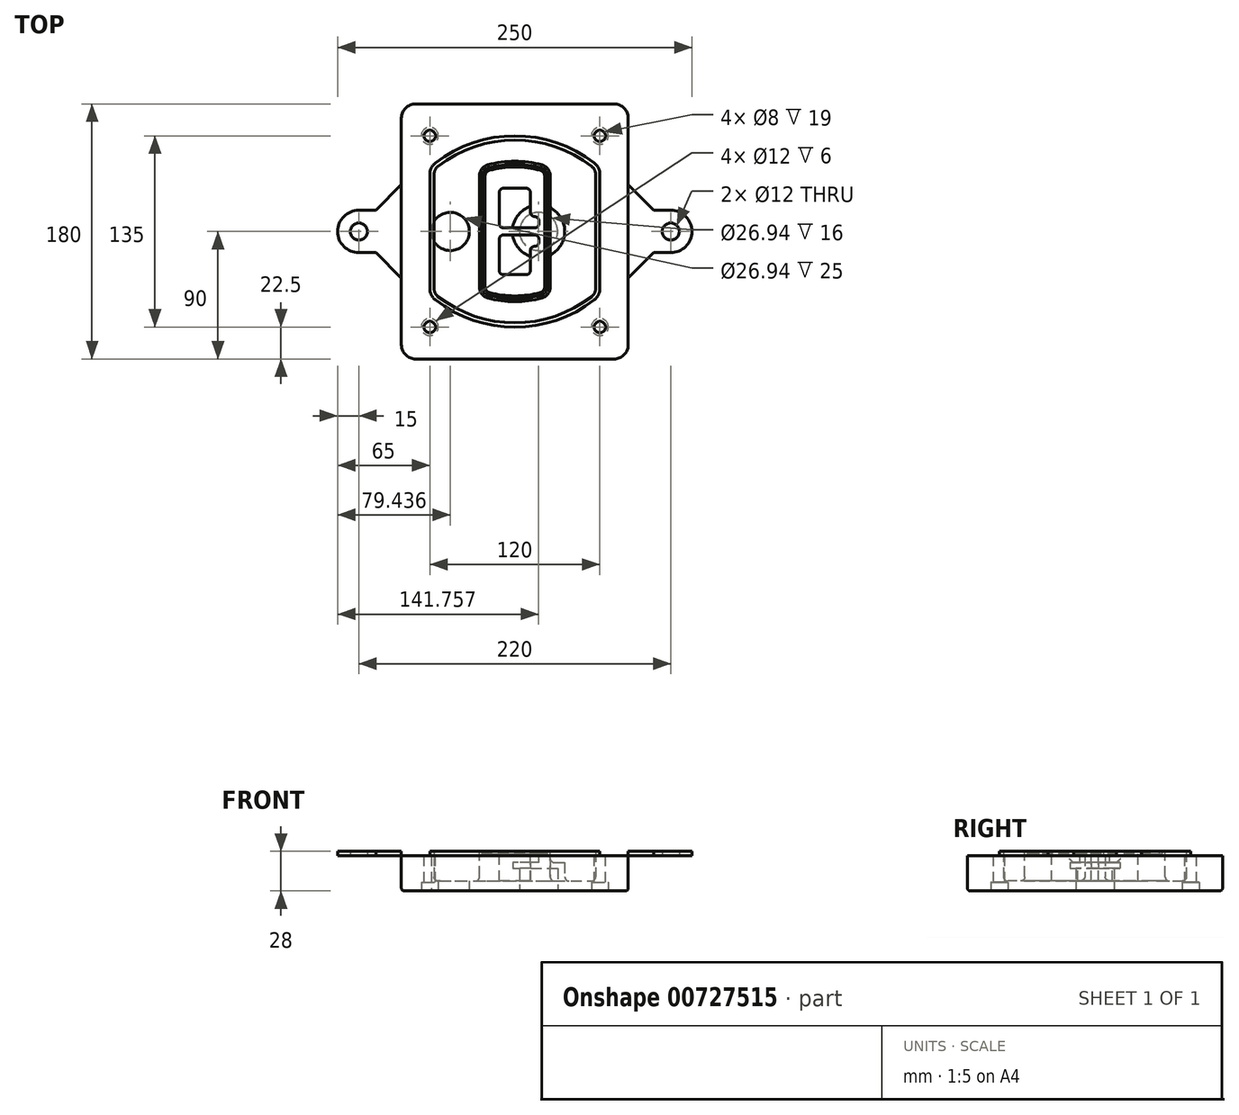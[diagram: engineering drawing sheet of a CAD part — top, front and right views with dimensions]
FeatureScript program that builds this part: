
annotation { "Feature Type Name" : "Feature", "Feature Type Description" : "" }
export const myFeature = defineFeature(function(context is Context, id is Id, definition is map)
    precondition{}
    {
        {
            var Q0;
            Q0=qCreatedBy(makeId("Top.planeOp"),FACE);
            var sketch = newSketch(context, id + "F0", { "sketchPlane" : qUnion([Q0])});
            skPoint(sketch, "E0.rect.middle", {"position": v(0, 0) * mm});
            skLineSegment(sketch, "E1.bottom", {"start": v(-70, -90) * mm, "end": v(70, -90) * mm});
            skLineSegment(sketch, "E1.top", {"start": v(-70, 90) * mm, "end": v(70, 90) * mm});
            skLineSegment(sketch, "E1.left", {"start": v(-80, -80) * mm, "end": v(-80, 80) * mm});
            skLineSegment(sketch, "E1.right", {"start": v(80, -80) * mm, "end": v(80, 80) * mm});
            skLineSegment(sketch, "E2", {"start": v(-80, 90) * mm, "end": v(80, -90) * mm, "construction": true});
            skLineSegment(sketch, "E3", {"start": v(80, 90) * mm, "end": v(-80, -90) * mm, "construction": true});
            skCircle(sketch, "E4", {"center": v(-60, 67.5) * mm, "radius": 4 * mm});
            skCircle(sketch, "E5", {"center": v(60, 67.5) * mm, "radius": 4 * mm});
            skCircle(sketch, "E6", {"center": v(60, -67.5) * mm, "radius": 4 * mm});
            skCircle(sketch, "E7", {"center": v(-60, -67.5) * mm, "radius": 4 * mm});
            skLineSegment(sketch, "E8", {"start": v(-60, 67.5) * mm, "end": v(60, 67.5) * mm, "construction": true});
            skLineSegment(sketch, "E9", {"start": v(60, 67.5) * mm, "end": v(60, -67.5) * mm, "construction": true});
            skLineSegment(sketch, "E10", {"start": v(60, -67.5) * mm, "end": v(-60, -67.5) * mm, "construction": true});
            skLineSegment(sketch, "E11", {"start": v(-60, -67.5) * mm, "end": v(-60, 67.5) * mm, "construction": true});
            skLineSegment(sketch, "E12", {"start": v(-60, 40.3) * mm, "end": v(-60, -40.3) * mm});
            skLineSegment(sketch, "E13", {"start": v(60, 40.3) * mm, "end": v(60, -40.3) * mm});
            skArc(sketch, "E14", {"start": v(56.15, 48.18) * mm, "mid": v(0, 67.5) * mm, "end": v(-56.15, 48.18) * mm});
            skArc(sketch, "E15", {"start": v(-56.15, -48.18) * mm, "mid": v(0, -67.5) * mm, "end": v(56.15, -48.18) * mm});
            skLineSegment(sketch, "E16", {"start": v(-60, 0) * mm, "end": v(60, 0) * mm, "construction": true});
            skPoint(sketch, "E17.visualSharp", {"position": v(-60, -45) * mm});
            skArc(sketch, "E17.filletArc", {"start": v(-60, -40.3) * mm, "mid": v(-58.99, -44.68) * mm, "end": v(-56.15, -48.18) * mm});
            skPoint(sketch, "E18.visualSharp", {"position": v(-60, 45) * mm});
            skArc(sketch, "E18.filletArc", {"start": v(-56.15, 48.18) * mm, "mid": v(-58.99, 44.68) * mm, "end": v(-60, 40.3) * mm});
            skPoint(sketch, "E19.visualSharp", {"position": v(60, 45) * mm});
            skArc(sketch, "E19.filletArc", {"start": v(60, 40.3) * mm, "mid": v(58.99, 44.68) * mm, "end": v(56.15, 48.18) * mm});
            skPoint(sketch, "E20.visualSharp", {"position": v(60, -45) * mm});
            skArc(sketch, "E20.filletArc", {"start": v(56.15, -48.18) * mm, "mid": v(58.99, -44.68) * mm, "end": v(60, -40.3) * mm});
            skPoint(sketch, "E21.visualSharp", {"position": v(-80, 90) * mm});
            skArc(sketch, "E21.filletArc", {"start": v(-70, 90) * mm, "mid": v(-77.07, 87.07) * mm, "end": v(-80, 80) * mm});
            skPoint(sketch, "E22.visualSharp", {"position": v(80, 90) * mm});
            skArc(sketch, "E22.filletArc", {"start": v(80, 80) * mm, "mid": v(77.07, 87.07) * mm, "end": v(70, 90) * mm});
            skPoint(sketch, "E23.visualSharp", {"position": v(80, -90) * mm});
            skArc(sketch, "E23.filletArc", {"start": v(70, -90) * mm, "mid": v(77.07, -87.07) * mm, "end": v(80, -80) * mm});
            skPoint(sketch, "E24.visualSharp", {"position": v(-80, -90) * mm});
            skArc(sketch, "E24.filletArc", {"start": v(-80, -80) * mm, "mid": v(-77.07, -87.07) * mm, "end": v(-70, -90) * mm});
            skArc(sketch, "E25.0", {"start": v(57, 40.3) * mm, "mid": v(56.3, 43.36) * mm, "end": v(54.3, 45.81) * mm});
            skLineSegment(sketch, "E25.1", {"start": v(57, 40.3) * mm, "end": v(57, -40.3) * mm});
            skArc(sketch, "E25.2", {"start": v(54.3, -45.81) * mm, "mid": v(56.3, -43.36) * mm, "end": v(57, -40.3) * mm});
            skArc(sketch, "E25.3", {"start": v(-54.3, -45.81) * mm, "mid": v(0, -64.5) * mm, "end": v(54.3, -45.81) * mm});
            skArc(sketch, "E25.4", {"start": v(-57, -40.3) * mm, "mid": v(-56.3, -43.36) * mm, "end": v(-54.3, -45.81) * mm});
            skArc(sketch, "E25.5", {"start": v(54.3, 45.81) * mm, "mid": v(0, 64.5) * mm, "end": v(-54.3, 45.81) * mm});
            skLineSegment(sketch, "E25.6", {"start": v(-57, 40.3) * mm, "end": v(-57, -40.3) * mm});
            skArc(sketch, "E25.7", {"start": v(-54.3, 45.81) * mm, "mid": v(-56.3, 43.36) * mm, "end": v(-57, 40.3) * mm});
            skArc(sketch, "E26.0", {"start": v(-58.62, 51.33) * mm, "mid": v(-62.58, 46.43) * mm, "end": v(-64, 40.3) * mm});
            skArc(sketch, "E26.1", {"start": v(58.62, 51.33) * mm, "mid": v(0, 71.5) * mm, "end": v(-58.62, 51.33) * mm});
            skArc(sketch, "E26.2", {"start": v(64, 40.3) * mm, "mid": v(62.58, 46.43) * mm, "end": v(58.62, 51.33) * mm});
            skLineSegment(sketch, "E26.3", {"start": v(64, 40.3) * mm, "end": v(64, -40.3) * mm});
            skArc(sketch, "E26.4", {"start": v(58.62, -51.33) * mm, "mid": v(62.58, -46.43) * mm, "end": v(64, -40.3) * mm});
            skLineSegment(sketch, "E26.5", {"start": v(-64, 40.3) * mm, "end": v(-64, -40.3) * mm});
            skArc(sketch, "E26.6", {"start": v(-58.62, -51.33) * mm, "mid": v(0, -71.5) * mm, "end": v(58.62, -51.33) * mm});
            skArc(sketch, "E26.7", {"start": v(-64, -40.3) * mm, "mid": v(-62.58, -46.43) * mm, "end": v(-58.62, -51.33) * mm});
            skSolve(sketch);
        }
        {
            var Q0;
            Q0=makeQuery(id+"F0.imprint","IMPRINT",FACE,{"disambiguationData":[TD([[makeQuery(id+"F0.imprint","IMPRINT",EDGE,{"derivedFrom":sQuery(id+"F0.wireOp",EDGE,"E1.bottom")}),1.0]])]});
            var Q1;
            Q1=makeQuery(id+"F0.imprint","IMPRINT",FACE,{"disambiguationData":[TD([[makeQuery(id+"F0.imprint","IMPRINT",EDGE,{"derivedFrom":sQuery(id+"F0.wireOp",EDGE,"E12")}),1.0]])]});
            var Q2;
            Q2=makeQuery(id+"F0.imprint","IMPRINT",FACE,{"disambiguationData":[TD([[makeQuery(id+"F0.imprint","IMPRINT",EDGE,{"derivedFrom":sQuery(id+"F0.wireOp",EDGE,"E25.0")}),1.0]])]});
            var Q3;
            Q3=makeQuery(id+"F0.imprint","IMPRINT",FACE,{"disambiguationData":[TD([[makeQuery(id+"F0.imprint","IMPRINT",EDGE,{"derivedFrom":sQuery(id+"F0.wireOp",EDGE,"E12")}),-1.0]])]});
            extrude(context, id + "F1", {"entities" : qUnion([Q0, Q1, Q2, Q3]), "oppositeDirection" : true, "depth" : 25 * mm});
        }
        {
            var Q0;
            Q0=makeQuery(id+"F0.imprint","IMPRINT",FACE,{"disambiguationData":[TD([[makeQuery(id+"F0.imprint","IMPRINT",EDGE,{"derivedFrom":sQuery(id+"F0.wireOp",EDGE,"E12")}),1.0]])]});
            extrude(context, id + "F2", {"entities" : qUnion([Q0]), "operationType" : NewBodyOperationType.ADD, "depth" : 3 * mm});
        }
        {
            var Q0;
            Q0=makeQuery(id+"F0.imprint","IMPRINT",FACE,{"disambiguationData":[TD([[makeQuery(id+"F0.imprint","IMPRINT",EDGE,{"derivedFrom":sQuery(id+"F0.wireOp",EDGE,"E25.0")}),1.0]])]});
            extrude(context, id + "F3", {"entities" : qUnion([Q0]), "operationType" : NewBodyOperationType.REMOVE, "oppositeDirection" : true, "depth" : 18 * mm});
        }
        {
            var Q0;
            Q0=makeQuery(id+"F2.opExtrude","CAP_FACE",FACE,{"disambiguationData":[OSD([sQuery(id+"F0.wireOp",EDGE,"E12"),sQuery(id+"F0.wireOp",EDGE,"E13"),sQuery(id+"F0.wireOp",EDGE,"E14"),sQuery(id+"F0.wireOp",EDGE,"E15"),sQuery(id+"F0.wireOp",EDGE,"E17.filletArc"),sQuery(id+"F0.wireOp",EDGE,"E18.filletArc"),sQuery(id+"F0.wireOp",EDGE,"E19.filletArc"),sQuery(id+"F0.wireOp",EDGE,"E20.filletArc"),sQuery(id+"F0.wireOp",EDGE,"E25.0"),sQuery(id+"F0.wireOp",EDGE,"E25.1"),sQuery(id+"F0.wireOp",EDGE,"E25.2"),sQuery(id+"F0.wireOp",EDGE,"E25.3"),sQuery(id+"F0.wireOp",EDGE,"E25.4"),sQuery(id+"F0.wireOp",EDGE,"E25.5"),sQuery(id+"F0.wireOp",EDGE,"E25.6"),sQuery(id+"F0.wireOp",EDGE,"E25.7")])],"isStart":false});
            var sketch = newSketch(context, id + "F4", { "sketchPlane" : qUnion([Q0])});
            skArc(sketch, "E27.0", {"start": v(-19.08, -46.97) * mm, "mid": v(0, -49.5) * mm, "end": v(19.08, -46.97) * mm});
            skArc(sketch, "E28.0", {"start": v(19.08, 46.97) * mm, "mid": v(0, 49.5) * mm, "end": v(-19.08, 46.97) * mm});
            skLineSegment(sketch, "E29", {"start": v(-25, 39.25) * mm, "end": v(-25, -39.25) * mm});
            skLineSegment(sketch, "E30", {"start": v(25, 39.25) * mm, "end": v(25, -39.25) * mm});
            skLineSegment(sketch, "E31", {"start": v(-25, 45.1) * mm, "end": v(25, 45.1) * mm, "construction": true});
            skLineSegment(sketch, "E32", {"start": v(-25, -45.1) * mm, "end": v(25, -45.1) * mm, "construction": true});
            skPoint(sketch, "E33.visualSharp", {"position": v(-25, 45.1) * mm});
            skArc(sketch, "E33.filletArc", {"start": v(-19.08, 46.97) * mm, "mid": v(-23.35, 44.11) * mm, "end": v(-25, 39.25) * mm});
            skPoint(sketch, "E34.visualSharp", {"position": v(25, 45.1) * mm});
            skArc(sketch, "E34.filletArc", {"start": v(25, 39.25) * mm, "mid": v(23.35, 44.11) * mm, "end": v(19.08, 46.97) * mm});
            skPoint(sketch, "E35.visualSharp", {"position": v(25, -45.1) * mm});
            skArc(sketch, "E35.filletArc", {"start": v(19.08, -46.97) * mm, "mid": v(23.35, -44.11) * mm, "end": v(25, -39.25) * mm});
            skPoint(sketch, "E36.visualSharp", {"position": v(-25, -45.1) * mm});
            skArc(sketch, "E36.filletArc", {"start": v(-25, -39.25) * mm, "mid": v(-23.35, -44.11) * mm, "end": v(-19.08, -46.97) * mm});
            skArc(sketch, "E37.0", {"start": v(54.3, 45.81) * mm, "mid": v(0, 64.5) * mm, "end": v(-54.3, 45.81) * mm});
            skArc(sketch, "E37.1", {"start": v(-54.3, 45.81) * mm, "mid": v(-56.3, 43.36) * mm, "end": v(-57, 40.3) * mm});
            skLineSegment(sketch, "E37.2", {"start": v(-57, 40.3) * mm, "end": v(-57, -40.3) * mm});
            skArc(sketch, "E37.3", {"start": v(-57, -40.3) * mm, "mid": v(-56.3, -43.36) * mm, "end": v(-54.3, -45.81) * mm});
            skArc(sketch, "E37.4", {"start": v(-54.3, -45.81) * mm, "mid": v(0, -64.5) * mm, "end": v(54.3, -45.81) * mm});
            skArc(sketch, "E37.5", {"start": v(54.3, -45.81) * mm, "mid": v(56.3, -43.36) * mm, "end": v(57, -40.3) * mm});
            skLineSegment(sketch, "E37.6", {"start": v(57, 40.3) * mm, "end": v(57, -40.3) * mm});
            skArc(sketch, "E37.7", {"start": v(57, 40.3) * mm, "mid": v(56.3, 43.36) * mm, "end": v(54.3, 45.81) * mm});
            skLineSegment(sketch, "E38.0", {"start": v(23, 39.25) * mm, "end": v(23, -39.25) * mm});
            skArc(sketch, "E38.1", {"start": v(18.56, -45.04) * mm, "mid": v(21.76, -42.9) * mm, "end": v(23, -39.25) * mm});
            skArc(sketch, "E38.2", {"start": v(-18.56, -45.04) * mm, "mid": v(0, -47.5) * mm, "end": v(18.56, -45.04) * mm});
            skArc(sketch, "E38.3", {"start": v(-23, -39.25) * mm, "mid": v(-21.76, -42.9) * mm, "end": v(-18.56, -45.04) * mm});
            skLineSegment(sketch, "E38.4", {"start": v(-23, 39.25) * mm, "end": v(-23, -39.25) * mm});
            skArc(sketch, "E38.5", {"start": v(23, 39.25) * mm, "mid": v(21.76, 42.9) * mm, "end": v(18.56, 45.04) * mm});
            skArc(sketch, "E38.6", {"start": v(-18.56, 45.04) * mm, "mid": v(-21.76, 42.9) * mm, "end": v(-23, 39.25) * mm});
            skArc(sketch, "E38.7", {"start": v(18.56, 45.04) * mm, "mid": v(0, 47.5) * mm, "end": v(-18.56, 45.04) * mm});
            skArc(sketch, "E39.0", {"start": v(21, 39.25) * mm, "mid": v(20.18, 41.68) * mm, "end": v(18.04, 43.1) * mm});
            skLineSegment(sketch, "E39.1", {"start": v(21, 39.25) * mm, "end": v(21, -39.25) * mm});
            skArc(sketch, "E39.2", {"start": v(18.04, -43.1) * mm, "mid": v(20.18, -41.68) * mm, "end": v(21, -39.25) * mm});
            skArc(sketch, "E39.3", {"start": v(-18.04, -43.1) * mm, "mid": v(0, -45.5) * mm, "end": v(18.04, -43.1) * mm});
            skArc(sketch, "E39.4", {"start": v(-21, -39.25) * mm, "mid": v(-20.18, -41.68) * mm, "end": v(-18.04, -43.1) * mm});
            skArc(sketch, "E39.5", {"start": v(18.04, 43.1) * mm, "mid": v(0, 45.5) * mm, "end": v(-18.04, 43.1) * mm});
            skLineSegment(sketch, "E39.6", {"start": v(-21, 39.25) * mm, "end": v(-21, -39.25) * mm});
            skArc(sketch, "E39.7", {"start": v(-18.04, 43.1) * mm, "mid": v(-20.18, 41.68) * mm, "end": v(-21, 39.25) * mm});
            skLineSegment(sketch, "E40", {"start": v(-25, 0) * mm, "end": v(25, 0) * mm, "construction": true});
            skLineSegment(sketch, "E41", {"start": v(-11, 5.5) * mm, "end": v(-11, 27.5) * mm});
            skLineSegment(sketch, "E42", {"start": v(-8, 30.5) * mm, "end": v(8, 30.5) * mm});
            skLineSegment(sketch, "E43", {"start": v(11, 27.5) * mm, "end": v(11, 13.5) * mm});
            skLineSegment(sketch, "E44", {"start": v(14, 10.5) * mm, "end": v(14, 10.5) * mm});
            skLineSegment(sketch, "E45", {"start": v(17, 7.5) * mm, "end": v(17, 5.5) * mm});
            skLineSegment(sketch, "E46", {"start": v(14, 2.5) * mm, "end": v(-8, 2.5) * mm});
            skPoint(sketch, "E47.visualSharp", {"position": v(-11, 30.5) * mm});
            skArc(sketch, "E47.filletArc", {"start": v(-8, 30.5) * mm, "mid": v(-10.12, 29.62) * mm, "end": v(-11, 27.5) * mm});
            skPoint(sketch, "E48.visualSharp", {"position": v(11, 30.5) * mm});
            skArc(sketch, "E48.filletArc", {"start": v(11, 27.5) * mm, "mid": v(10.12, 29.62) * mm, "end": v(8, 30.5) * mm});
            skPoint(sketch, "E49.visualSharp", {"position": v(11, 10.5) * mm});
            skArc(sketch, "E49.filletArc", {"start": v(11, 13.5) * mm, "mid": v(11.88, 11.38) * mm, "end": v(14, 10.5) * mm});
            skPoint(sketch, "E50.visualSharp", {"position": v(17, 10.5) * mm});
            skArc(sketch, "E50.filletArc", {"start": v(17, 7.5) * mm, "mid": v(16.12, 9.62) * mm, "end": v(14, 10.5) * mm});
            skPoint(sketch, "E51.visualSharp", {"position": v(17, 2.5) * mm});
            skArc(sketch, "E51.filletArc", {"start": v(14, 2.5) * mm, "mid": v(16.12, 3.38) * mm, "end": v(17, 5.5) * mm});
            skPoint(sketch, "E52.visualSharp", {"position": v(-11, 2.5) * mm});
            skArc(sketch, "E52.filletArc", {"start": v(-11, 5.5) * mm, "mid": v(-10.12, 3.38) * mm, "end": v(-8, 2.5) * mm});
            skLineSegment(sketch, "E53.0.MirrorCS", {"start": v(14, -2.5) * mm, "end": v(-8, -2.5) * mm});
            skArc(sketch, "E54.0.MirrorCS", {"start": v(-11, -5.5) * mm, "mid": v(-10.12, -3.38) * mm, "end": v(-8, -2.5) * mm});
            skLineSegment(sketch, "E55.0.MirrorCS", {"start": v(-11, -5.5) * mm, "end": v(-11, -27.5) * mm});
            skArc(sketch, "E56.0.MirrorCS", {"start": v(-8, -30.5) * mm, "mid": v(-10.12, -29.62) * mm, "end": v(-11, -27.5) * mm});
            skLineSegment(sketch, "E57.0.MirrorCS", {"start": v(-8, -30.5) * mm, "end": v(8, -30.5) * mm});
            skArc(sketch, "E58.0.MirrorCS", {"start": v(11, -27.5) * mm, "mid": v(10.12, -29.62) * mm, "end": v(8, -30.5) * mm});
            skLineSegment(sketch, "E59.0.MirrorCS", {"start": v(11, -27.5) * mm, "end": v(11, -13.5) * mm});
            skArc(sketch, "E60.0.MirrorCS", {"start": v(11, -13.5) * mm, "mid": v(11.88, -11.38) * mm, "end": v(14, -10.5) * mm});
            skArc(sketch, "E61.0.MirrorCS", {"start": v(17, -7.5) * mm, "mid": v(16.12, -9.62) * mm, "end": v(14, -10.5) * mm});
            skLineSegment(sketch, "E62.0.MirrorCS", {"start": v(17, -7.5) * mm, "end": v(17, -5.5) * mm});
            skArc(sketch, "E63.0.MirrorCS", {"start": v(14, -2.5) * mm, "mid": v(16.12, -3.38) * mm, "end": v(17, -5.5) * mm});
            skSolve(sketch);
        }
        {
            var Q0;
            Q0=makeQuery(id+"F4.imprint","IMPRINT",FACE,{"disambiguationData":[TD([[makeQuery(id+"F4.imprint","IMPRINT",EDGE,{"derivedFrom":sQuery(id+"F4.wireOp",EDGE,"E27.0")}),1.0]])]});
            var Q1;
            Q1=makeQuery(id+"F4.imprint","IMPRINT",FACE,{"disambiguationData":[TD([[makeQuery(id+"F4.imprint","IMPRINT",EDGE,{"derivedFrom":sQuery(id+"F4.wireOp",EDGE,"E38.0")}),-1.0]])]});
            var Q2;
            Q2=makeQuery(id+"F4.imprint","IMPRINT",FACE,{"disambiguationData":[TD([[makeQuery(id+"F4.imprint","IMPRINT",EDGE,{"derivedFrom":sQuery(id+"F4.wireOp",EDGE,"E39.0")}),1.0]])]});
            extrude(context, id + "F5", {"entities" : qUnion([Q0, Q1, Q2]), "operationType" : NewBodyOperationType.ADD, "endBound" : BoundingType.UP_TO_NEXT, "oppositeDirection" : true, "depth" : 25 * mm});
        }
        {
            var Q0;
            Q0=makeQuery(id+"F4.imprint","IMPRINT",FACE,{"disambiguationData":[TD([[makeQuery(id+"F4.imprint","IMPRINT",EDGE,{"derivedFrom":sQuery(id+"F4.wireOp",EDGE,"E38.0")}),-1.0]])]});
            extrude(context, id + "F6", {"entities" : qUnion([Q0]), "operationType" : NewBodyOperationType.REMOVE, "oppositeDirection" : true, "depth" : 2 * mm});
        }
        {
            var Q0;
            Q0=makeQuery(id+"F1.opExtrude","CAP_FACE",FACE,{"disambiguationData":[OSD([sQuery(id+"F0.wireOp",EDGE,"E1.bottom"),sQuery(id+"F0.wireOp",EDGE,"E1.top"),sQuery(id+"F0.wireOp",EDGE,"E1.left"),sQuery(id+"F0.wireOp",EDGE,"E1.right"),sQuery(id+"F0.wireOp",EDGE,"E4"),sQuery(id+"F0.wireOp",EDGE,"E5"),sQuery(id+"F0.wireOp",EDGE,"E6"),sQuery(id+"F0.wireOp",EDGE,"E7"),sQuery(id+"F0.wireOp",EDGE,"E21.filletArc"),sQuery(id+"F0.wireOp",EDGE,"E22.filletArc"),sQuery(id+"F0.wireOp",EDGE,"E23.filletArc"),sQuery(id+"F0.wireOp",EDGE,"E24.filletArc")])],"isStart":false});
            var sketch = newSketch(context, id + "F7", { "sketchPlane" : qUnion([Q0])});
            skCircle(sketch, "E64", {"center": v(16.76, 0) * mm, "radius": 13.47 * mm});
            skCircle(sketch, "E65", {"center": v(-45.56, 0) * mm, "radius": 13.47 * mm});
            skLineSegment(sketch, "E66", {"start": v(80, 0) * mm, "end": v(-80, 0) * mm});
            skCircle(sketch, "E67", {"center": v(16.76, 0) * mm, "radius": 18.47 * mm});
            skCircle(sketch, "E68", {"center": v(60, -67.5) * mm, "radius": 6 * mm});
            skCircle(sketch, "E69", {"center": v(-60, -67.5) * mm, "radius": 6 * mm});
            skCircle(sketch, "E70", {"center": v(-60, 67.5) * mm, "radius": 6 * mm});
            skCircle(sketch, "E71", {"center": v(60, 67.5) * mm, "radius": 6 * mm});
            skSolve(sketch);
        }
        {
            var Q0;
            {var subQ1=sQuery(id+"F7.wireOp",EDGE,"E66");var subQ4=sQuery(id+"F7.wireOp",EDGE,"E64");var subQ6=makeQuery(id+"F7.imprint","INTERSECT",VERTEX,{"disambiguationData":[OD(0.0)],"derivedFrom":[subQ4,subQ1]});Q0=makeQuery(id+"F7.imprint","IMPRINT",FACE,{"disambiguationData":[TD([[makeQuery(id+"F7.imprint","IMPRINT",EDGE,{"disambiguationData":[TD([[subQ6,-1.0]])],"derivedFrom":subQ4}),-1.0]])]});}
            var Q1;
            {var subQ0=sQuery(id+"F7.wireOp",EDGE,"E66");var subQ1=sQuery(id+"F7.wireOp",EDGE,"E64");var subQ3=makeQuery(id+"F7.imprint","INTERSECT",VERTEX,{"disambiguationData":[OD(0.0)],"derivedFrom":[subQ1,subQ0]});Q1=makeQuery(id+"F7.imprint","IMPRINT",FACE,{"disambiguationData":[TD([[makeQuery(id+"F7.imprint","IMPRINT",EDGE,{"disambiguationData":[TD([[subQ3,-1.0]])],"derivedFrom":subQ1}),1.0]])]});}
            var Q2;
            {var subQ0=sQuery(id+"F7.wireOp",EDGE,"E66");var subQ1=sQuery(id+"F7.wireOp",EDGE,"E64");var subQ3=makeQuery(id+"F7.imprint","INTERSECT",VERTEX,{"disambiguationData":[OD(0.0)],"derivedFrom":[subQ1,subQ0]});Q2=makeQuery(id+"F7.imprint","IMPRINT",FACE,{"disambiguationData":[TD([[makeQuery(id+"F7.imprint","IMPRINT",EDGE,{"disambiguationData":[TD([[subQ3,1.0]])],"derivedFrom":subQ1}),1.0]])]});}
            var Q3;
            {var subQ1=sQuery(id+"F7.wireOp",EDGE,"E66");var subQ4=sQuery(id+"F7.wireOp",EDGE,"E64");var subQ6=makeQuery(id+"F7.imprint","INTERSECT",VERTEX,{"disambiguationData":[OD(0.0)],"derivedFrom":[subQ4,subQ1]});Q3=makeQuery(id+"F7.imprint","IMPRINT",FACE,{"disambiguationData":[TD([[makeQuery(id+"F7.imprint","IMPRINT",EDGE,{"disambiguationData":[TD([[subQ6,1.0]])],"derivedFrom":subQ4}),-1.0]])]});}
            extrude(context, id + "F8", {"entities" : qUnion([Q0, Q1, Q2, Q3]), "operationType" : NewBodyOperationType.ADD, "oppositeDirection" : true, "depth" : 20 * mm});
        }
        {
            var Q0;
            {var subQ0=sQuery(id+"F7.wireOp",EDGE,"E66");var subQ1=sQuery(id+"F7.wireOp",EDGE,"E64");var subQ3=makeQuery(id+"F7.imprint","INTERSECT",VERTEX,{"disambiguationData":[OD(0.0)],"derivedFrom":[subQ1,subQ0]});Q0=makeQuery(id+"F7.imprint","IMPRINT",FACE,{"disambiguationData":[TD([[makeQuery(id+"F7.imprint","IMPRINT",EDGE,{"disambiguationData":[TD([[subQ3,-1.0]])],"derivedFrom":subQ1}),1.0]])]});}
            var Q1;
            {var subQ0=sQuery(id+"F7.wireOp",EDGE,"E66");var subQ1=sQuery(id+"F7.wireOp",EDGE,"E64");var subQ3=makeQuery(id+"F7.imprint","INTERSECT",VERTEX,{"disambiguationData":[OD(0.0)],"derivedFrom":[subQ1,subQ0]});Q1=makeQuery(id+"F7.imprint","IMPRINT",FACE,{"disambiguationData":[TD([[makeQuery(id+"F7.imprint","IMPRINT",EDGE,{"disambiguationData":[TD([[subQ3,1.0]])],"derivedFrom":subQ1}),1.0]])]});}
            extrude(context, id + "F9", {"entities" : qUnion([Q0, Q1]), "operationType" : NewBodyOperationType.REMOVE, "oppositeDirection" : true, "depth" : 16 * mm});
        }
        {
            var Q0;
            {var subQ0=sQuery(id+"F7.wireOp",EDGE,"E66");var subQ1=sQuery(id+"F7.wireOp",EDGE,"E65");var subQ3=makeQuery(id+"F7.imprint","INTERSECT",VERTEX,{"disambiguationData":[OD(0.0)],"derivedFrom":[subQ1,subQ0]});Q0=makeQuery(id+"F7.imprint","IMPRINT",FACE,{"disambiguationData":[TD([[makeQuery(id+"F7.imprint","IMPRINT",EDGE,{"disambiguationData":[TD([[subQ3,-1.0]])],"derivedFrom":subQ1}),1.0]])]});}
            var Q1;
            {var subQ0=sQuery(id+"F7.wireOp",EDGE,"E66");var subQ1=sQuery(id+"F7.wireOp",EDGE,"E65");var subQ3=makeQuery(id+"F7.imprint","INTERSECT",VERTEX,{"disambiguationData":[OD(0.0)],"derivedFrom":[subQ1,subQ0]});Q1=makeQuery(id+"F7.imprint","IMPRINT",FACE,{"disambiguationData":[TD([[makeQuery(id+"F7.imprint","IMPRINT",EDGE,{"disambiguationData":[TD([[subQ3,1.0]])],"derivedFrom":subQ1}),1.0]])]});}
            extrude(context, id + "F10", {"entities" : qUnion([Q0, Q1]), "operationType" : NewBodyOperationType.REMOVE, "oppositeDirection" : true, "depth" : 25 * mm});
        }
        {
            var Q0;
            Q0=makeQuery(id+"F7.imprint","IMPRINT",FACE,{"disambiguationData":[TD([[makeQuery(id+"F7.imprint","IMPRINT",EDGE,{"derivedFrom":sQuery(id+"F7.wireOp",EDGE,"E68")}),1.0]])]});
            var Q1;
            Q1=makeQuery(id+"F7.imprint","IMPRINT",FACE,{"disambiguationData":[TD([[makeQuery(id+"F7.imprint","IMPRINT",EDGE,{"derivedFrom":makeQuery(id+"F1.opExtrude","CAP_EDGE",EDGE,{"disambiguationData":[OSD([sQuery(id+"F0.wireOp",EDGE,"E5")])],"isStart":false})}),-1.0]])]});
            var Q2;
            Q2=makeQuery(id+"F7.imprint","IMPRINT",FACE,{"disambiguationData":[TD([[makeQuery(id+"F7.imprint","IMPRINT",EDGE,{"derivedFrom":sQuery(id+"F7.wireOp",EDGE,"E69")}),1.0]])]});
            var Q3;
            Q3=makeQuery(id+"F7.imprint","IMPRINT",FACE,{"disambiguationData":[TD([[makeQuery(id+"F7.imprint","IMPRINT",EDGE,{"derivedFrom":makeQuery(id+"F1.opExtrude","CAP_EDGE",EDGE,{"disambiguationData":[OSD([sQuery(id+"F0.wireOp",EDGE,"E4")])],"isStart":false})}),-1.0]])]});
            var Q4;
            Q4=makeQuery(id+"F7.imprint","IMPRINT",FACE,{"disambiguationData":[TD([[makeQuery(id+"F7.imprint","IMPRINT",EDGE,{"derivedFrom":sQuery(id+"F7.wireOp",EDGE,"E70")}),1.0]])]});
            var Q5;
            Q5=makeQuery(id+"F7.imprint","IMPRINT",FACE,{"disambiguationData":[TD([[makeQuery(id+"F7.imprint","IMPRINT",EDGE,{"derivedFrom":makeQuery(id+"F1.opExtrude","CAP_EDGE",EDGE,{"disambiguationData":[OSD([sQuery(id+"F0.wireOp",EDGE,"E7")])],"isStart":false})}),-1.0]])]});
            var Q6;
            Q6=makeQuery(id+"F7.imprint","IMPRINT",FACE,{"disambiguationData":[TD([[makeQuery(id+"F7.imprint","IMPRINT",EDGE,{"derivedFrom":sQuery(id+"F7.wireOp",EDGE,"E71")}),1.0]])]});
            var Q7;
            Q7=makeQuery(id+"F7.imprint","IMPRINT",FACE,{"disambiguationData":[TD([[makeQuery(id+"F7.imprint","IMPRINT",EDGE,{"derivedFrom":makeQuery(id+"F1.opExtrude","CAP_EDGE",EDGE,{"disambiguationData":[OSD([sQuery(id+"F0.wireOp",EDGE,"E6")])],"isStart":false})}),-1.0]])]});
            extrude(context, id + "F11", {"entities" : qUnion([Q0, Q1, Q2, Q3, Q4, Q5, Q6, Q7]), "operationType" : NewBodyOperationType.REMOVE, "oppositeDirection" : true, "depth" : 6 * mm});
        }
        {
            var Q0;
            Q0=makeQuery(id+"F9.boolean.opBoolean","COPY",FACE,{"derivedFrom":makeQuery(id+"F9.opExtrude","CAP_FACE",FACE,{"disambiguationData":[OSD([sQuery(id+"F7.wireOp",EDGE,"E64")])],"isStart":false})});
            var sketch = newSketch(context, id + "F12", { "sketchPlane" : qUnion([Q0])});
            skArc(sketch, "E72.0", {"start": v(11, 17.55) * mm, "mid": v(2.57, 11.82) * mm, "end": v(-1.54, 2.5) * mm});
            skArc(sketch, "E72.1", {"start": v(-1.54, -2.5) * mm, "mid": v(2.57, -11.82) * mm, "end": v(11, -17.55) * mm});
            skLineSegment(sketch, "E73", {"start": v(-1.54, -2.5) * mm, "end": v(14, -2.5) * mm});
            skLineSegment(sketch, "E74.0", {"start": v(14, 2.5) * mm, "end": v(-1.54, 2.5) * mm});
            skArc(sketch, "E74.1", {"start": v(14, 2.5) * mm, "mid": v(16.12, 3.38) * mm, "end": v(17, 5.5) * mm});
            skLineSegment(sketch, "E74.2", {"start": v(17, 7.5) * mm, "end": v(17, 5.5) * mm});
            skArc(sketch, "E74.3", {"start": v(17, 7.5) * mm, "mid": v(16.12, 9.62) * mm, "end": v(14, 10.5) * mm});
            skArc(sketch, "E74.4", {"start": v(11, 13.5) * mm, "mid": v(11.88, 11.38) * mm, "end": v(14, 10.5) * mm});
            skLineSegment(sketch, "E74.5", {"start": v(11, 17.55) * mm, "end": v(11, 13.5) * mm});
            skLineSegment(sketch, "E74.7", {"start": v(14, -2.5) * mm, "end": v(-1.54, -2.5) * mm});
            skArc(sketch, "E74.8", {"start": v(14, -2.5) * mm, "mid": v(16.12, -3.38) * mm, "end": v(17, -5.5) * mm});
            skLineSegment(sketch, "E74.9", {"start": v(17, -7.5) * mm, "end": v(17, -5.5) * mm});
            skArc(sketch, "E74.10", {"start": v(17, -7.5) * mm, "mid": v(16.12, -9.62) * mm, "end": v(14, -10.5) * mm});
            skArc(sketch, "E74.11", {"start": v(11, -13.5) * mm, "mid": v(11.88, -11.38) * mm, "end": v(14, -10.5) * mm});
            skLineSegment(sketch, "E74.12", {"start": v(11, -17.55) * mm, "end": v(11, -13.5) * mm});
            skPoint(sketch, "E75.orphan", {"position": v(11, -27.5) * mm});
            skPoint(sketch, "E76.orphan", {"position": v(-8, -2.5) * mm});
            skPoint(sketch, "E77.orphan", {"position": v(-8, 2.5) * mm});
            skPoint(sketch, "E78.orphan", {"position": v(11, 27.5) * mm});
            skSolve(sketch);
        }
        {
            var Q0;
            {var subQ7=sQuery(id+"F12.wireOp",EDGE,"E72.0");var subQ14=sQuery(id+"F12.wireOp",EDGE,"E72.1");var subQ16=sQuery(id+"F12.wireOp",EDGE,"E74.1");var subQ18=sQuery(id+"F12.wireOp",EDGE,"E74.8");Q0=qUnion([makeQuery(id+"F12.imprint","IMPRINT",FACE,{"disambiguationData":[TD([[makeQuery(id+"F12.imprint","IMPRINT",EDGE,{"derivedFrom":subQ7}),1.0]])]}),makeQuery(id+"F12.imprint","IMPRINT",FACE,{"disambiguationData":[TD([[makeQuery(id+"F12.imprint","IMPRINT",EDGE,{"derivedFrom":subQ14}),1.0]])]}),makeQuery(id+"F12.imprint","IMPRINT",FACE,{"disambiguationData":[TD([[makeQuery(id+"F12.imprint","IMPRINT",EDGE,{"derivedFrom":subQ16}),1.0]])]}),makeQuery(id+"F12.imprint","IMPRINT",FACE,{"disambiguationData":[TD([[makeQuery(id+"F12.imprint","IMPRINT",EDGE,{"derivedFrom":subQ18}),-1.0]])]})]);}
            var Q1;
            Q1=makeQuery(id+"F5.boolean.opBoolean","SPLIT",FACE,{"disambiguationData":[TD([makeQuery(id+"F5.opExtrude","SWEPT_FACE",FACE,{"disambiguationData":[OSD([sQuery(id+"F4.wireOp",EDGE,"E41")])]})])],"derivedFrom":makeQuery(id+"F3.boolean.opBoolean","COPY",FACE,{"derivedFrom":makeQuery(id+"F3.opExtrude","CAP_FACE",FACE,{"disambiguationData":[OSD([sQuery(id+"F0.wireOp",EDGE,"E25.0"),sQuery(id+"F0.wireOp",EDGE,"E25.1"),sQuery(id+"F0.wireOp",EDGE,"E25.2"),sQuery(id+"F0.wireOp",EDGE,"E25.3"),sQuery(id+"F0.wireOp",EDGE,"E25.4"),sQuery(id+"F0.wireOp",EDGE,"E25.5"),sQuery(id+"F0.wireOp",EDGE,"E25.6"),sQuery(id+"F0.wireOp",EDGE,"E25.7")])],"isStart":false})})});
            extrude(context, id + "F13", {"entities" : qUnion([Q0]), "operationType" : NewBodyOperationType.REMOVE, "endBound" : BoundingType.UP_TO_SURFACE, "endBoundEntityFace" : qUnion([Q1]), "depth" : 25 * mm});
        }
        {
            var Q0;
            Q0=makeQuery(id+"F3.boolean.opBoolean","COPY",EDGE,{"derivedFrom":makeQuery(id+"F3.opExtrude","CAP_EDGE",EDGE,{"disambiguationData":[OSD([sQuery(id+"F0.wireOp",EDGE,"E25.6")])],"isStart":false})});
            var Q1;
            Q1=makeQuery(id+"F8.boolean.opBoolean","INTERSECT",EDGE,{"derivedFrom":[makeQuery(id+"F5.opExtrude","SWEPT_FACE",FACE,{"disambiguationData":[OSD([sQuery(id+"F4.wireOp",EDGE,"E30")])]}),makeQuery(id+"F8.opExtrude","CAP_FACE",FACE,{"disambiguationData":[OSD([sQuery(id+"F7.wireOp",EDGE,"E67")])],"isStart":false})]});
            var Q2;
            Q2=makeQuery(id+"F8.boolean.opBoolean","INTERSECT",EDGE,{"disambiguationData":[OD(1.0)],"derivedFrom":[makeQuery(id+"F5.opExtrude","SWEPT_FACE",FACE,{"disambiguationData":[OSD([sQuery(id+"F4.wireOp",EDGE,"E30")])]}),makeQuery(id+"F8.opExtrude","SWEPT_FACE",FACE,{"disambiguationData":[OSD([sQuery(id+"F7.wireOp",EDGE,"E67")])]})]});
            var Q3;
            {var subQ0=sQuery(id+"F4.wireOp",EDGE,"E30");Q3=makeQuery(id+"F8.boolean.opBoolean","SPLIT",EDGE,{"disambiguationData":[TD([makeQuery(id+"F5.opExtrude","SWEPT_FACE",FACE,{"disambiguationData":[OSD([sQuery(id+"F4.wireOp",EDGE,"E35.filletArc")])]})])],"derivedFrom":makeQuery(id+"F5.opExtrude","CAP_EDGE",EDGE,{"disambiguationData":[OSD([subQ0])],"isStart":false})});}
            var Q4;
            {var subQ0=sQuery(id+"F0.wireOp",EDGE,"E25.7");var subQ1=sQuery(id+"F0.wireOp",EDGE,"E25.1");var subQ2=sQuery(id+"F0.wireOp",EDGE,"E25.6");var subQ3=sQuery(id+"F0.wireOp",EDGE,"E25.5");var subQ4=sQuery(id+"F0.wireOp",EDGE,"E25.4");var subQ5=sQuery(id+"F0.wireOp",EDGE,"E25.0");var subQ6=sQuery(id+"F0.wireOp",EDGE,"E25.2");var subQ7=sQuery(id+"F0.wireOp",EDGE,"E25.3");Q4=makeQuery(id+"F8.boolean.opBoolean","INTERSECT",EDGE,{"derivedFrom":[makeQuery(id+"F5.boolean.opBoolean","SPLIT",FACE,{"disambiguationData":[TD([makeQuery(id+"F2.opExtrude","SWEPT_FACE",FACE,{"disambiguationData":[OSD([subQ5])]})])],"derivedFrom":makeQuery(id+"F3.boolean.opBoolean","COPY",FACE,{"derivedFrom":makeQuery(id+"F3.opExtrude","CAP_FACE",FACE,{"disambiguationData":[OSD([subQ5,subQ1,subQ6,subQ7,subQ4,subQ3,subQ2,subQ0])],"isStart":false})})}),makeQuery(id+"F8.opExtrude","SWEPT_FACE",FACE,{"disambiguationData":[OSD([sQuery(id+"F7.wireOp",EDGE,"E67")])]})]});}
            var Q5;
            Q5=makeQuery(id+"F8.boolean.opBoolean","INTERSECT",EDGE,{"disambiguationData":[OD(0.0)],"derivedFrom":[makeQuery(id+"F5.opExtrude","SWEPT_FACE",FACE,{"disambiguationData":[OSD([sQuery(id+"F4.wireOp",EDGE,"E30")])]}),makeQuery(id+"F8.opExtrude","SWEPT_FACE",FACE,{"disambiguationData":[OSD([sQuery(id+"F7.wireOp",EDGE,"E67")])]})]});
            fillet(context, id + "F14", {"entities" : qUnion([Q0, Q1, Q2, Q3, Q4, Q5]), "radius" : 3 * mm, "tangentPropagation" : true, "allowEdgeOverflow" : false});
        }
        {
            var Q0;
            Q0=makeQuery(id+"F1.opExtrude","CAP_EDGE",EDGE,{"disambiguationData":[OSD([sQuery(id+"F0.wireOp",EDGE,"E1.bottom")])],"isStart":false});
            fillet(context, id + "F15", {"entities" : qUnion([Q0]), "radius" : 2 * mm, "tangentPropagation" : true, "allowEdgeOverflow" : false});
        }
        {
            var Q0;
            {var subQ0=sQuery(id+"F0.wireOp",EDGE,"E21.filletArc");var subQ1=sQuery(id+"F0.wireOp",EDGE,"E7");var subQ2=sQuery(id+"F0.wireOp",EDGE,"E6");var subQ3=sQuery(id+"F0.wireOp",EDGE,"E5");var subQ4=sQuery(id+"F0.wireOp",EDGE,"E4");var subQ5=sQuery(id+"F0.wireOp",EDGE,"E22.filletArc");var subQ6=sQuery(id+"F0.wireOp",EDGE,"E1.bottom");var subQ7=sQuery(id+"F0.wireOp",EDGE,"E1.right");var subQ8=sQuery(id+"F0.wireOp",EDGE,"E1.top");var subQ9=sQuery(id+"F0.wireOp",EDGE,"E1.left");var subQ10=sQuery(id+"F0.wireOp",EDGE,"E23.filletArc");var subQ11=sQuery(id+"F0.wireOp",EDGE,"E24.filletArc");Q0=makeQuery(id+"F2.boolean.opBoolean","SPLIT",FACE,{"disambiguationData":[TD([makeQuery(id+"F1.opExtrude","SWEPT_FACE",FACE,{"disambiguationData":[OSD([subQ6])]})])],"derivedFrom":makeQuery(id+"F1.opExtrude","CAP_FACE",FACE,{"disambiguationData":[OSD([subQ6,subQ8,subQ9,subQ7,subQ4,subQ3,subQ2,subQ1,subQ0,subQ5,subQ10,subQ11])],"isStart":true})});}
            var sketch = newSketch(context, id + "F16", { "sketchPlane" : qUnion([Q0])});
            skLineSegment(sketch, "E79", {"start": v(-80, -33) * mm, "end": v(-98, -15) * mm});
            skLineSegment(sketch, "E80", {"start": v(-80, 33) * mm, "end": v(-98, 15) * mm});
            skLineSegment(sketch, "E81", {"start": v(-110, -15) * mm, "end": v(-98, -15) * mm});
            skLineSegment(sketch, "E82", {"start": v(-98, 15) * mm, "end": v(-110, 15) * mm});
            skArc(sketch, "E83", {"start": v(-110, 15) * mm, "mid": v(-125, 0) * mm, "end": v(-110, -15) * mm});
            skCircle(sketch, "E84", {"center": v(-110, 0) * mm, "radius": 6 * mm});
            skLineSegment(sketch, "E85", {"start": v(-110, 0) * mm, "end": v(-80, 0) * mm, "construction": true});
            skLineSegment(sketch, "E86", {"start": v(0, 90) * mm, "end": v(0, -90) * mm, "construction": true});
            skLineSegment(sketch, "E87.MirrorCS", {"start": v(80, 33) * mm, "end": v(98, 15) * mm});
            skLineSegment(sketch, "E88.MirrorCS", {"start": v(98, 15) * mm, "end": v(110, 15) * mm});
            skArc(sketch, "E89.MirrorCS", {"start": v(110, 15) * mm, "mid": v(125, 0) * mm, "end": v(110, -15) * mm});
            skLineSegment(sketch, "E90.MirrorCS", {"start": v(110, -15) * mm, "end": v(98, -15) * mm});
            skLineSegment(sketch, "E91.MirrorCS", {"start": v(80, -33) * mm, "end": v(98, -15) * mm});
            skCircle(sketch, "E92.MirrorC", {"center": v(110, 0) * mm, "radius": 6 * mm});
            skLineSegment(sketch, "E93.MirrorCS", {"start": v(110, 0) * mm, "end": v(80, 0) * mm, "construction": true});
            skSolve(sketch);
        }
        {
            var Q0;
            Q0=makeQuery(id+"F16.imprint","IMPRINT",FACE,{"disambiguationData":[TD([[makeQuery(id+"F16.imprint","IMPRINT",EDGE,{"derivedFrom":makeQuery(id+"F1.opExtrude","CAP_EDGE",EDGE,{"disambiguationData":[OSD([sQuery(id+"F0.wireOp",EDGE,"E1.bottom")])],"isStart":true})}),1.0]])]});
            var sketch = newSketch(context, id + "F17", { "sketchPlane" : qUnion([Q0])});
            skSolve(sketch);
        }
        {
            var Q0;
            {var subQ1=sQuery(id+"F16.wireOp",EDGE,"E79");Q0=makeQuery(id+"F16.imprint","IMPRINT",FACE,{"disambiguationData":[TD([[makeQuery(id+"F16.imprint","IMPRINT",EDGE,{"derivedFrom":subQ1}),-1.0]])]});}
            var Q1;
            Q1=makeQuery(id+"F17.imprint","IMPRINT",FACE,{"disambiguationData":[TD([[makeQuery(id+"F17.imprint","IMPRINT",EDGE,{"derivedFrom":makeQuery(id+"F16.imprint","IMPRINT",EDGE,{"derivedFrom":makeQuery(id+"F1.opExtrude","CAP_EDGE",EDGE,{"disambiguationData":[OSD([sQuery(id+"F0.wireOp",EDGE,"E1.bottom")])],"isStart":true})})}),1.0]])]});
            var Q2;
            {var subQ0=sQuery(id+"F16.wireOp",EDGE,"E87.MirrorCS");Q2=makeQuery(id+"F16.imprint","IMPRINT",FACE,{"disambiguationData":[TD([[makeQuery(id+"F16.imprint","IMPRINT",EDGE,{"derivedFrom":subQ0}),-1.0]])]});}
            var Q3;
            Q3=makeQuery(id+"F2.opExtrude","CAP_FACE",FACE,{"disambiguationData":[OSD([sQuery(id+"F0.wireOp",EDGE,"E12"),sQuery(id+"F0.wireOp",EDGE,"E13"),sQuery(id+"F0.wireOp",EDGE,"E14"),sQuery(id+"F0.wireOp",EDGE,"E15"),sQuery(id+"F0.wireOp",EDGE,"E17.filletArc"),sQuery(id+"F0.wireOp",EDGE,"E18.filletArc"),sQuery(id+"F0.wireOp",EDGE,"E19.filletArc"),sQuery(id+"F0.wireOp",EDGE,"E20.filletArc"),sQuery(id+"F0.wireOp",EDGE,"E25.0"),sQuery(id+"F0.wireOp",EDGE,"E25.1"),sQuery(id+"F0.wireOp",EDGE,"E25.2"),sQuery(id+"F0.wireOp",EDGE,"E25.3"),sQuery(id+"F0.wireOp",EDGE,"E25.4"),sQuery(id+"F0.wireOp",EDGE,"E25.5"),sQuery(id+"F0.wireOp",EDGE,"E25.6"),sQuery(id+"F0.wireOp",EDGE,"E25.7")])],"isStart":false});
            extrude(context, id + "F18", {"entities" : qUnion([Q0, Q1, Q2]), "endBound" : BoundingType.UP_TO_SURFACE, "depth" : 25 * mm, "endBoundEntityFace" : qUnion([Q3]), "offsetDistance" : 25 * mm});
        }
    });
